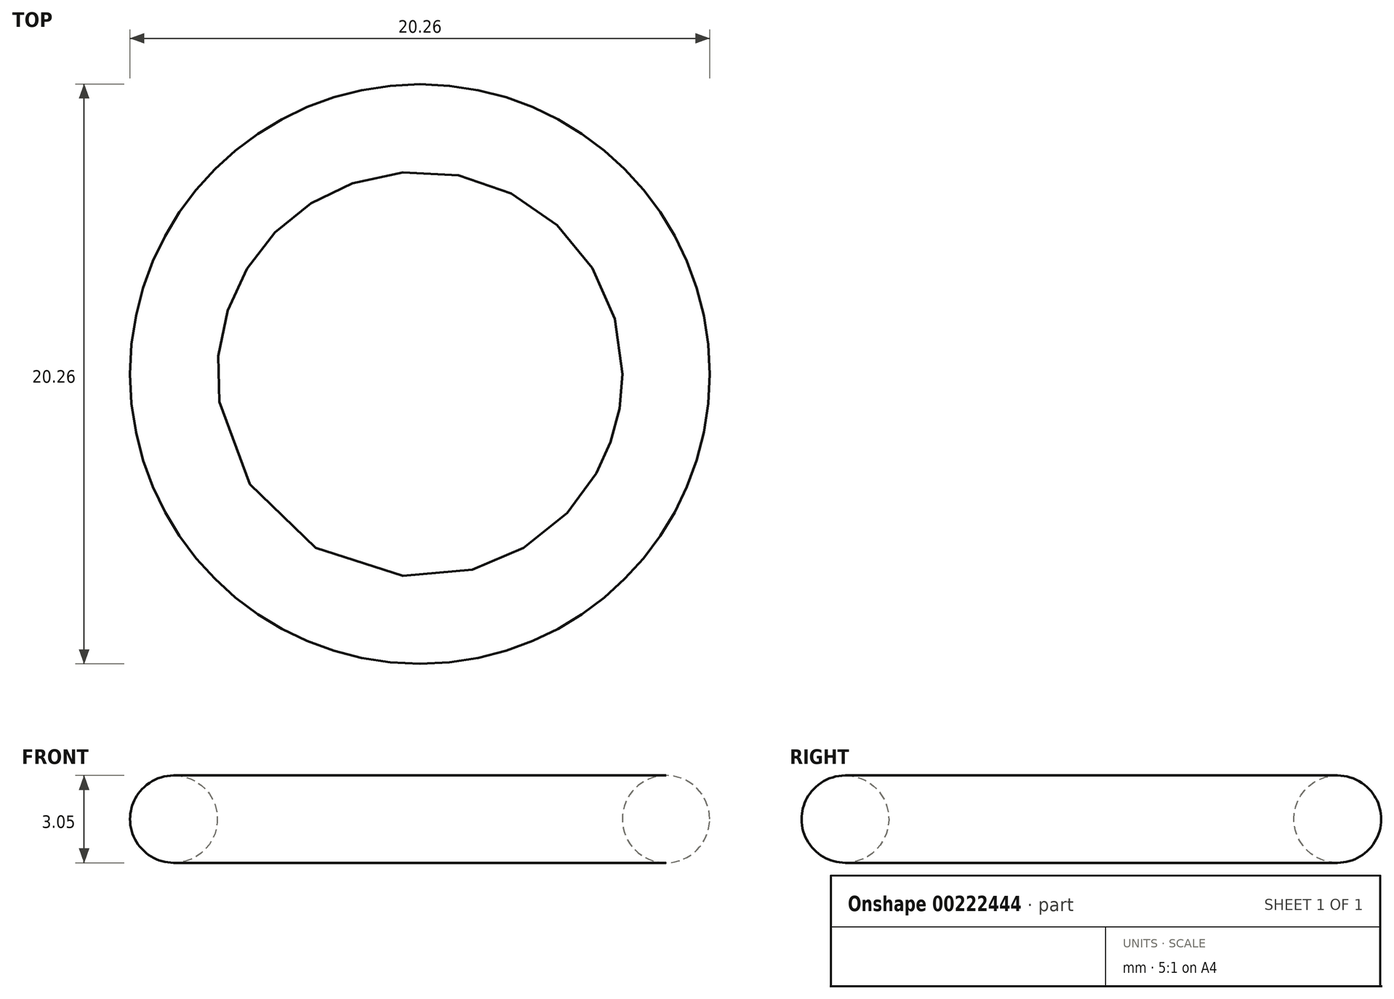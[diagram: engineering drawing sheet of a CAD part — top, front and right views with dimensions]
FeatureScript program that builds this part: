
annotation { "Feature Type Name" : "Feature", "Feature Type Description" : "" }
export const myFeature = defineFeature(function(context is Context, id is Id, definition is map)
    precondition{}
    {
        {
            var Q0;
            Q0=qCreatedBy(makeId("Front.planeOp"),FACE);
            var sketch = newSketch(context, id + "F0", { "sketchPlane" : qUnion([Q0])});
            skLineSegment(sketch, "E0", {"start": v(0, 29.04) * mm, "end": v(0, -31.35) * mm, "construction": true});
            skCircle(sketch, "E1", {"center": v(-8.6, 4.77) * mm, "radius": 1.52 * mm});
            skSolve(sketch);
        }
        {
            var Q0;
            Q0 = qSketchRegion(id + "F0", true);
            var Q1;
            Q1=sQuery(id+"F0.wireOp",EDGE,"E0");
            revolve(context, id + "F1", {"entities" : qUnion([Q0]), "axis" : qUnion([Q1]), "revolveType" : RevolveType.FULL});
        }
    });
